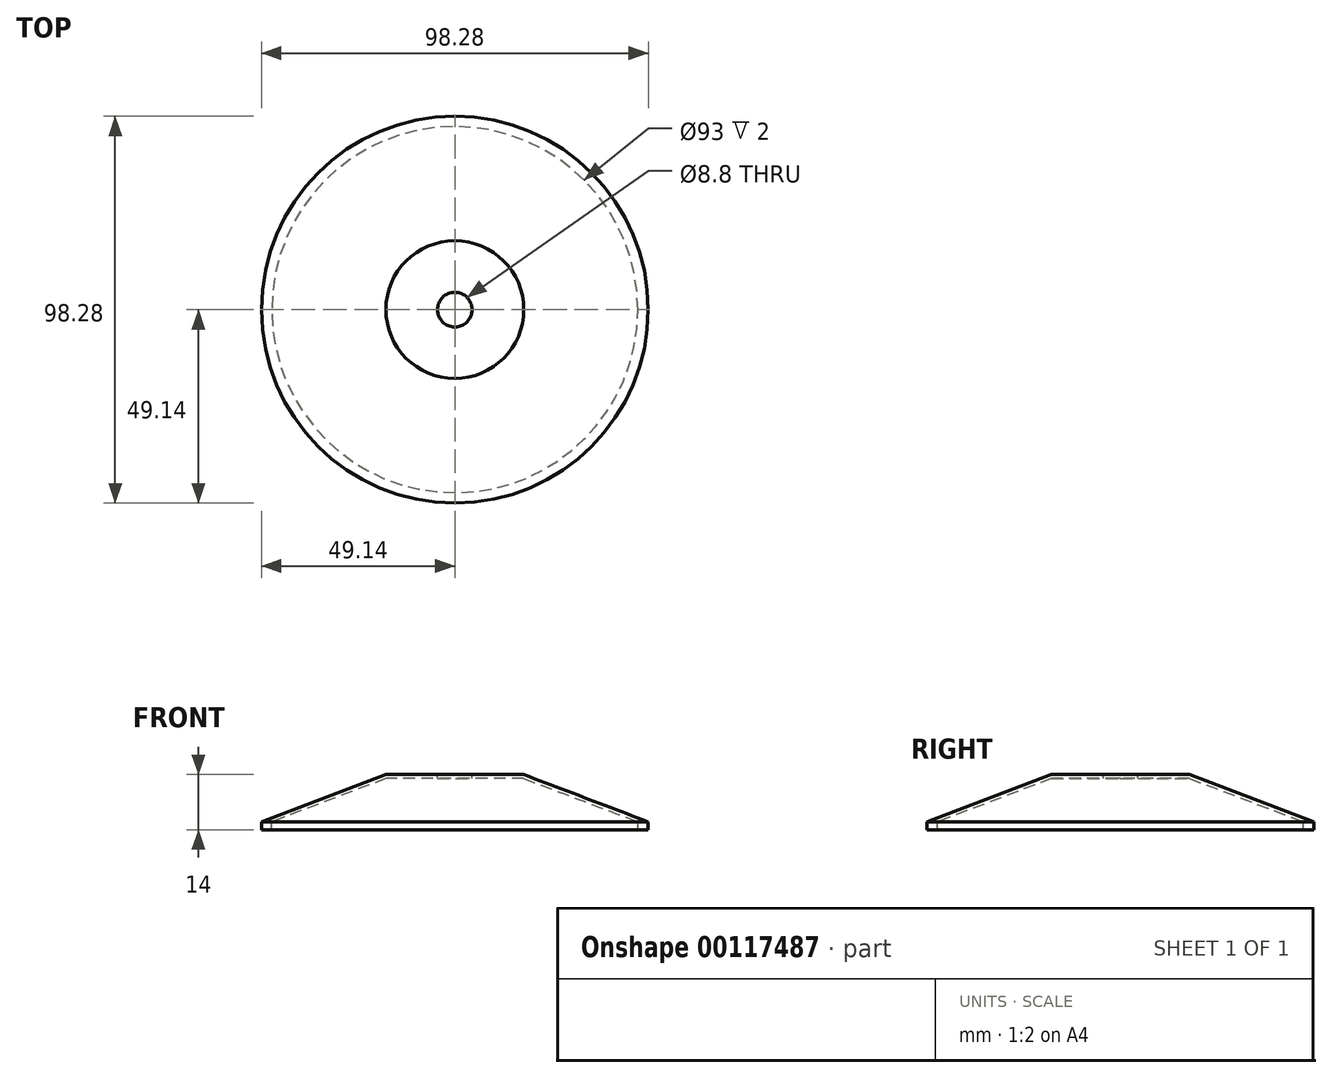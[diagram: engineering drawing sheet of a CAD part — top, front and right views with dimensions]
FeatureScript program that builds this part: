
annotation { "Feature Type Name" : "Feature", "Feature Type Description" : "" }
export const myFeature = defineFeature(function(context is Context, id is Id, definition is map)
    precondition{}
    {
        {
            var Q0;
            Q0=qCreatedBy(makeId("Right.planeOp"),FACE);
            var sketch = newSketch(context, id + "F0", { "sketchPlane" : qUnion([Q0])});
            skLineSegment(sketch, "E0", {"start": v(46.5, 0) * mm, "end": v(46.5, 0) * mm});
            skLineSegment(sketch, "E1", {"start": v(46.5, 0) * mm, "end": v(46.5, 2) * mm});
            skLineSegment(sketch, "E2", {"start": v(46.5, 2) * mm, "end": v(17.5, 13) * mm});
            skLineSegment(sketch, "E3", {"start": v(17.5, 13) * mm, "end": v(0, 13) * mm});
            skLineSegment(sketch, "E4", {"start": v(0, 14) * mm, "end": v(0, 13) * mm});
            skLineSegment(sketch, "E5", {"start": v(0, 14) * mm, "end": v(17.5, 14) * mm});
            skLineSegment(sketch, "E6", {"start": v(17.5, 14) * mm, "end": v(49.14, 2) * mm});
            skLineSegment(sketch, "E7", {"start": v(49.14, 2) * mm, "end": v(49.14, 0) * mm});
            skLineSegment(sketch, "E8", {"start": v(46.5, 0) * mm, "end": v(49.14, 0) * mm});
            skSolve(sketch);
        }
        {
            var Q0;
            Q0 = qSketchRegion(id + "F0", true);
            var Q1;
            Q1 = qConstructionFilter(qBodyType(qCreatedBy(id + "F0" ,EDGE), BodyType.WIRE), ConstructionObject.NO);
            var Q2;
            Q2=sQuery(id+"F0.wireOp",EDGE,"E4");
            revolve(context, id + "F1", {"entities" : qUnion([Q0]), "surfaceEntities" : qUnion([Q1]), "axis" : qUnion([Q2]), "revolveType" : RevolveType.FULL});
        }
        {
            var Q0;
            Q0=makeQuery(id+"F1.opRevolve","SWEPT_FACE",FACE,{"disambiguationData":[OSD([sQuery(id+"F0.wireOp",EDGE,"E5")])]});
            var sketch = newSketch(context, id + "F2", { "sketchPlane" : qUnion([Q0])});
            skPoint(sketch, "E9", {"position": v(0, 0) * mm});
            skSolve(sketch);
        }
        {
            var Q0;
            Q0=sQuery(id+"F2.wireOp",VERTEX,"E9");
            var Q1;
            Q1=makeQuery(id+"F1.opRevolve","SWEPT_BODY",BODY,{"disambiguationData":[OSD([sQuery(id+"F0.wireOp",EDGE,"E1"),sQuery(id+"F0.wireOp",EDGE,"E2"),sQuery(id+"F0.wireOp",EDGE,"E3"),sQuery(id+"F0.wireOp",EDGE,"E4"),sQuery(id+"F0.wireOp",EDGE,"E5"),sQuery(id+"F0.wireOp",EDGE,"E6"),sQuery(id+"F0.wireOp",EDGE,"E7"),sQuery(id+"F0.wireOp",EDGE,"E8")])]});
            hole(context, id + "F3", {"style" : HoleStyle.SIMPLE, "endStyle" : HoleEndStyle.THROUGH, "standardTappedOrClearance" : lookupTablePath({ "standard" : "ISO", "fit" : "Normal", "size" : "M8", "type" : "Clearance" }), "standardBlindInLast" : lookupTablePath({ "fit" : "Standard", "standard" : "ISO", "size" : "M8", "type" : "Clearance" }), "holeDiameter" : 8.8 * mm, "locations" : qUnion([Q0]), "scope" : qUnion([Q1]), "isTappedThrough" : true});
        }
    });
